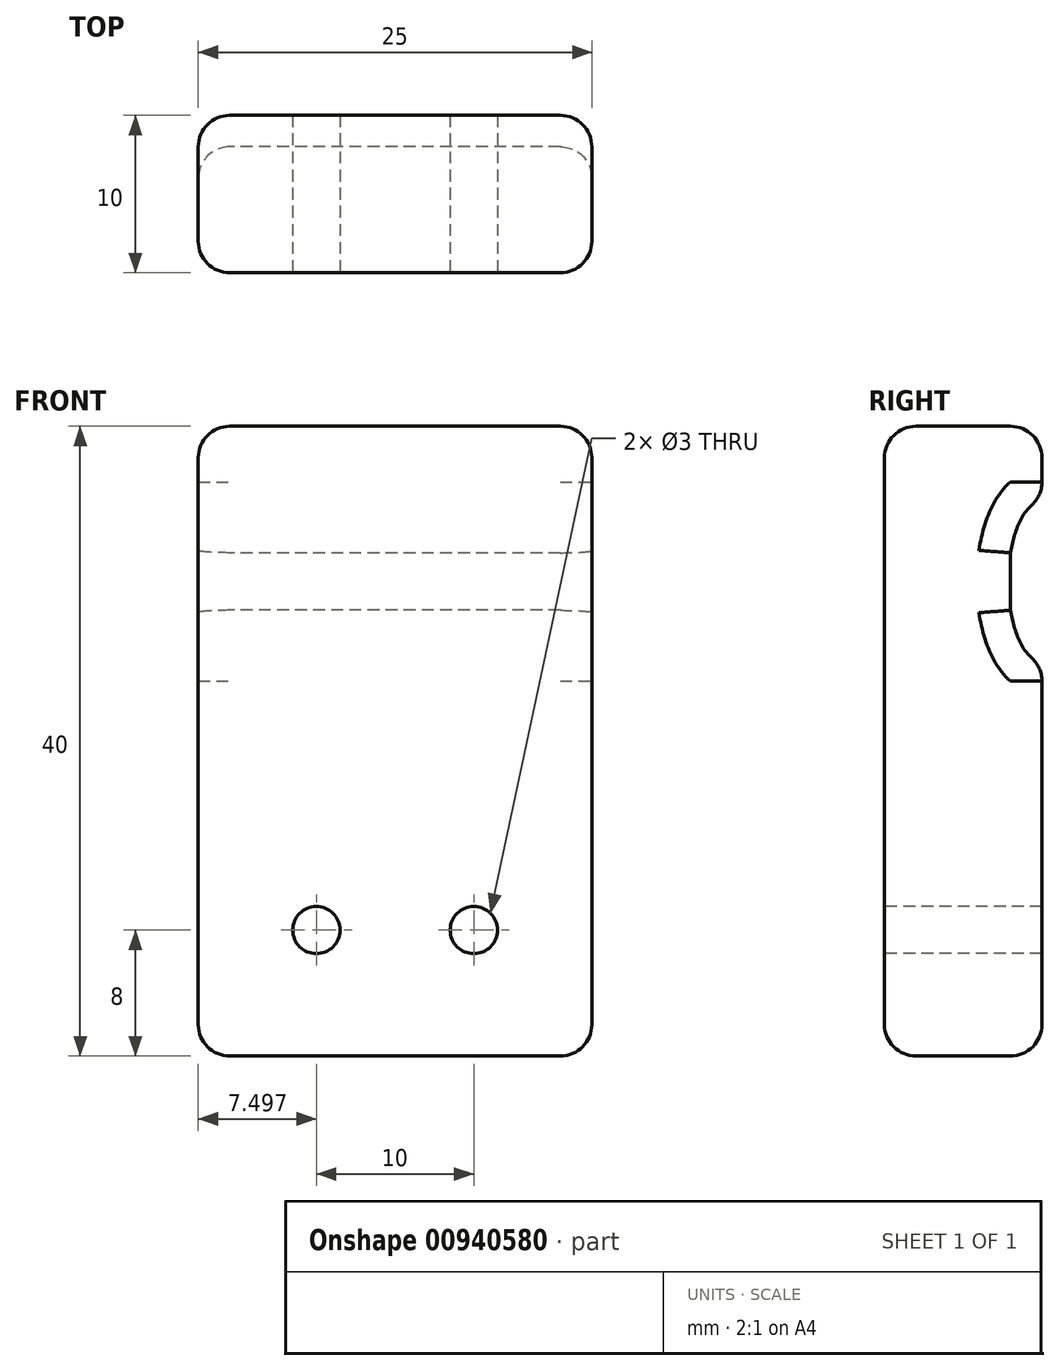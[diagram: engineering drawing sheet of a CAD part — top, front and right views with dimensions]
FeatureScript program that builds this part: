
annotation { "Feature Type Name" : "Feature", "Feature Type Description" : "" }
export const myFeature = defineFeature(function(context is Context, id is Id, definition is map)
    precondition{}
    {
        {
            var Q0;
            Q0=qCreatedBy(makeId("Top.planeOp"),FACE);
            var sketch = newSketch(context, id + "F0", { "sketchPlane" : qUnion([Q0])});
            skLineSegment(sketch, "E0.bottom", {"start": v(-9.85, 6.5) * mm, "end": v(11.15, 6.5) * mm});
            skLineSegment(sketch, "E0.top", {"start": v(-9.85, -3.5) * mm, "end": v(11.15, -3.5) * mm});
            skLineSegment(sketch, "E0.left", {"start": v(-11.85, 4.5) * mm, "end": v(-11.85, -1.5) * mm});
            skLineSegment(sketch, "E0.right", {"start": v(13.15, 4.5) * mm, "end": v(13.15, -1.5) * mm});
            skPoint(sketch, "E1.visualSharp", {"position": v(-11.85, -3.5) * mm});
            skArc(sketch, "E1.filletArc", {"start": v(-11.85, -1.5) * mm, "mid": v(-11.27, -2.91) * mm, "end": v(-9.85, -3.5) * mm});
            skPoint(sketch, "E2.visualSharp", {"position": v(13.15, -3.5) * mm});
            skArc(sketch, "E2.filletArc", {"start": v(11.15, -3.5) * mm, "mid": v(12.56, -2.91) * mm, "end": v(13.15, -1.5) * mm});
            skPoint(sketch, "E3.visualSharp", {"position": v(-11.85, 6.5) * mm});
            skArc(sketch, "E3.filletArc", {"start": v(-9.85, 6.5) * mm, "mid": v(-11.27, 5.91) * mm, "end": v(-11.85, 4.5) * mm});
            skPoint(sketch, "E4.visualSharp", {"position": v(13.15, 6.5) * mm});
            skArc(sketch, "E4.filletArc", {"start": v(13.15, 4.5) * mm, "mid": v(12.56, 5.91) * mm, "end": v(11.15, 6.5) * mm});
            skSolve(sketch);
        }
        {
            var Q0;
            Q0=makeQuery(id+"F0.imprint","IMPRINT",FACE,{"disambiguationData":[TD([[makeQuery(id+"F0.imprint","IMPRINT",EDGE,{"derivedFrom":sQuery(id+"F0.wireOp",EDGE,"E0.bottom")}),-1.0]])]});
            extrude(context, id + "F1", {"entities" : qUnion([Q0]), "depth" : 40 * mm, "offsetDistance" : 25 * mm});
        }
        {
            var Q0;
            Q0=makeQuery(id+"F1.opExtrude","SWEPT_FACE",FACE,{"disambiguationData":[OSD([sQuery(id+"F0.wireOp",EDGE,"E0.top")])]});
            var sketch = newSketch(context, id + "F2", { "sketchPlane" : qUnion([Q0])});
            skCircle(sketch, "E5", {"center": v(5.65, 8) * mm, "radius": 1.5 * mm});
            skCircle(sketch, "E6", {"center": v(-4.35, 8) * mm, "radius": 1.5 * mm});
            skSolve(sketch);
        }
        {
            var Q0;
            Q0=makeQuery(id+"F2.imprint","IMPRINT",FACE,{"disambiguationData":[TD([[makeQuery(id+"F2.imprint","IMPRINT",EDGE,{"derivedFrom":sQuery(id+"F2.wireOp",EDGE,"E6")}),1.0]])]});
            var Q1;
            Q1=makeQuery(id+"F2.imprint","IMPRINT",FACE,{"disambiguationData":[TD([[makeQuery(id+"F2.imprint","IMPRINT",EDGE,{"derivedFrom":sQuery(id+"F2.wireOp",EDGE,"E5")}),1.0]])]});
            extrude(context, id + "F3", {"entities" : qUnion([Q0, Q1]), "operationType" : NewBodyOperationType.REMOVE, "endBound" : BoundingType.UP_TO_NEXT, "oppositeDirection" : true, "depth" : 25 * mm, "offsetDistance" : 25 * mm});
        }
        {
            var Q0;
            Q0=makeQuery(id+"F1.opExtrude","CAP_EDGE",EDGE,{"disambiguationData":[OSD([sQuery(id+"F0.wireOp",EDGE,"E1.filletArc")])],"isStart":true});
            fillet(context, id + "F4", {"entities" : qUnion([Q0]), "radius" : 2 * mm, "tangentPropagation" : true, "allowEdgeOverflow" : false});
        }
        {
            var Q0;
            Q0=makeQuery(id+"F1.opExtrude","SWEPT_FACE",FACE,{"disambiguationData":[OSD([sQuery(id+"F0.wireOp",EDGE,"E0.left")])]});
            var sketch = newSketch(context, id + "F5", { "sketchPlane" : qUnion([Q0])});
            skEllipticalArc(sketch, "E7", {});
            skLineSegment(sketch, "E8", {"start": v(-6.57, 25.01) * mm, "end": v(-6.57, 35.26) * mm});
            const initialGuessF5  = {"E7": [-0.0065736593678593636, 0.03013538382947445, 0, 1, 0.00512402318418026, 0.0022187997449263966, 3.141592653589793, 0]};
            skSetInitialGuess(sketch, initialGuessF5);
            skSolve(sketch);
        }
        {
            var Q0;
            {var subQ0=sQuery(id+"F5.wireOp",EDGE,"E8");Q0=makeQuery(id+"F5.imprint","IMPRINT",FACE,{"disambiguationData":[TD([[makeQuery(id+"F5.imprint","IMPRINT",EDGE,{"derivedFrom":subQ0}),-1.0]])]});}
            extrude(context, id + "F6", {"entities" : qUnion([Q0]), "operationType" : NewBodyOperationType.REMOVE, "endBound" : BoundingType.THROUGH_ALL, "oppositeDirection" : true, "depth" : 25 * mm, "offsetDistance" : 25 * mm});
        }
        {
            var Q0;
            {var subQ0=sQuery(id+"F0.wireOp",EDGE,"E3.filletArc");var subQ1=sQuery(id+"F0.wireOp",EDGE,"E0.left");Q0=makeQuery(id+"F6.boolean.opBoolean","MERGE",EDGE,{"derivedFrom":[makeQuery(id+"F1.opExtrude","SWEPT_EDGE",EDGE,{"disambiguationData":[OSD([subQ1,subQ0])]})],"fromTools":[makeQuery(id+"F6.opExtrude","CAP_EDGE",EDGE,{"disambiguationData":[OSD([subQ1,subQ0])],"isStart":true})]});}
            var Q1;
            {var subQ0=sQuery(id+"F0.wireOp",EDGE,"E0.right");Q1=makeQuery(id+"F6.boolean.opBoolean","SPLIT",EDGE,{"disambiguationData":[topologyDisambiguationEdgeConnected([makeQuery(id+"F1.opExtrude","SWEPT_FACE",FACE,{"disambiguationData":[OSD([subQ0])]}),makeQuery(id+"F6.opExtrude","SWEPT_FACE",FACE,{"disambiguationData":[OSD([sQuery(id+"F0.wireOp",EDGE,"E0.left"),sQuery(id+"F0.wireOp",EDGE,"E3.filletArc")])]})])],"derivedFrom":makeQuery(id+"F1.opExtrude","SWEPT_EDGE",EDGE,{"disambiguationData":[OSD([subQ0,sQuery(id+"F0.wireOp",EDGE,"E4.filletArc")])]})});}
            var Q2;
            {var subQ1=sQuery(id+"F0.wireOp",EDGE,"E0.bottom");var subQ2=sQuery(id+"F0.wireOp",EDGE,"E3.filletArc");Q2=makeQuery(id+"F6.boolean.opBoolean","SPLIT",FACE,{"disambiguationData":[TD([makeQuery(id+"F4.opFillet","BLEND_FACE",FACE,{"disambiguationData":[OSD([subQ1])]})])],"derivedFrom":makeQuery(id+"F1.opExtrude","SWEPT_FACE",FACE,{"disambiguationData":[OSD([subQ2])]})});}
            var Q3;
            {var subQ0=sQuery(id+"F5.wireOp",EDGE,"E7");var subQ1=sQuery(id+"F0.wireOp",EDGE,"E3.filletArc");Q3=makeQuery(id+"F6.boolean.opBoolean","INTERSECT",EDGE,{"derivedFrom":[makeQuery(id+"F1.opExtrude","SWEPT_FACE",FACE,{"disambiguationData":[OSD([subQ1])]}),makeQuery(id+"F6.opExtrude","SWEPT_FACE",FACE,{"disambiguationData":[OSD([subQ0]),TDD([makeQuery(id+"F5.imprint","IMPRINT",EDGE,{"disambiguationData":[TD([[makeQuery(id+"F5.imprint","INTERSECT",VERTEX,{"disambiguationData":[OD(1.0)],"derivedFrom":[subQ0,sQuery(id+"F5.wireOp",EDGE,"E8")]}),1.0]])],"derivedFrom":subQ0})])]})]});}
            var Q4;
            {var subQ0=sQuery(id+"F5.wireOp",EDGE,"E7");Q4=makeQuery(id+"F6.boolean.opBoolean","INTERSECT",EDGE,{"derivedFrom":[makeQuery(id+"F1.opExtrude","SWEPT_FACE",FACE,{"disambiguationData":[OSD([sQuery(id+"F0.wireOp",EDGE,"E4.filletArc")])]}),makeQuery(id+"F6.opExtrude","SWEPT_FACE",FACE,{"disambiguationData":[OSD([subQ0]),TDD([makeQuery(id+"F5.imprint","IMPRINT",EDGE,{"disambiguationData":[TD([[makeQuery(id+"F5.imprint","INTERSECT",VERTEX,{"disambiguationData":[OD(1.0)],"derivedFrom":[subQ0,sQuery(id+"F5.wireOp",EDGE,"E8")]}),1.0]])],"derivedFrom":subQ0})])]})]});}
            fillet(context, id + "F7", {"entities" : qUnion([Q0, Q1, Q2, Q3, Q4]), "radius" : 2 * mm, "tangentPropagation" : true, "allowEdgeOverflow" : false});
        }
        {
            var Q0;
            Q0=makeQuery(id+"F1.opExtrude","CAP_EDGE",EDGE,{"disambiguationData":[OSD([sQuery(id+"F0.wireOp",EDGE,"E3.filletArc")])],"isStart":false});
            var Q1;
            Q1=makeQuery(id+"F1.opExtrude","CAP_EDGE",EDGE,{"disambiguationData":[OSD([sQuery(id+"F0.wireOp",EDGE,"E0.bottom")])],"isStart":false});
            fillet(context, id + "F8", {"entities" : qUnion([Q0, Q1]), "radius" : 2 * mm, "tangentPropagation" : true, "allowEdgeOverflow" : false});
        }
    });
